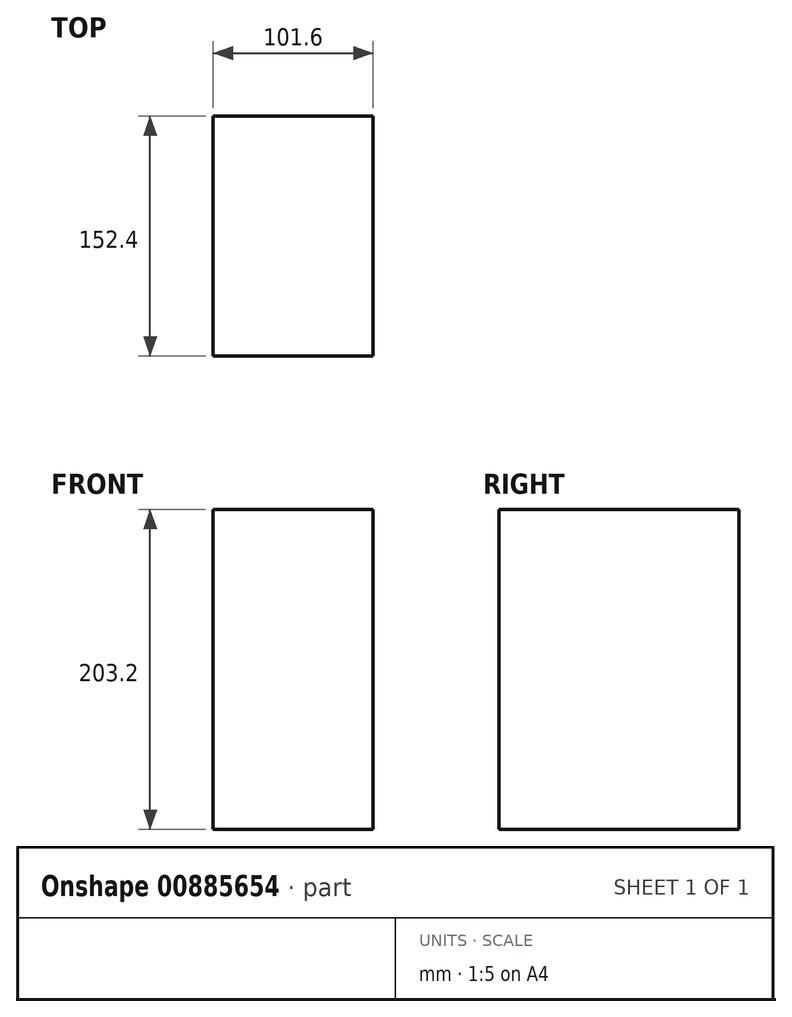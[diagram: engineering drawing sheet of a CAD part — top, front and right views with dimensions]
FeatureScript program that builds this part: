
annotation { "Feature Type Name" : "Feature", "Feature Type Description" : "" }
export const myFeature = defineFeature(function(context is Context, id is Id, definition is map)
    precondition{}
    {
        {
            var Q0;
            Q0=qCreatedBy(makeId("Top.planeOp"),FACE);
            var sketch = newSketch(context, id + "F0", { "sketchPlane" : qUnion([Q0])});
            skLineSegment(sketch, "E0.bottom", {"start": v(0, 0) * mm, "end": v(101.6, 0) * mm});
            skLineSegment(sketch, "E0.top", {"start": v(0, 152.4) * mm, "end": v(101.6, 152.4) * mm});
            skLineSegment(sketch, "E0.left", {"start": v(0, 0) * mm, "end": v(0, 152.4) * mm});
            skLineSegment(sketch, "E0.right", {"start": v(101.6, 0) * mm, "end": v(101.6, 152.4) * mm});
            skSolve(sketch);
        }
        {
            var Q0;
            Q0 = qSketchRegion(id + "F0", true);
            extrude(context, id + "F1", {"entities" : qUnion([Q0]), "depth" : 101.6 * mm, "offsetDistance" : 25.4 * mm});
        }
        {
            var Q0;
            Q0=makeQuery(id+"F1.opExtrude","SWEPT_BODY",BODY,{"disambiguationData":[OSD([sQuery(id+"F0.wireOp",EDGE,"E0.bottom"),sQuery(id+"F0.wireOp",EDGE,"E0.top"),sQuery(id+"F0.wireOp",EDGE,"E0.left"),sQuery(id+"F0.wireOp",EDGE,"E0.right")])]});
            var Q1;
            Q1=makeQuery(id+"F1.opExtrude","CAP_FACE",FACE,{"disambiguationData":[OSD([sQuery(id+"F0.wireOp",EDGE,"E0.bottom"),sQuery(id+"F0.wireOp",EDGE,"E0.top"),sQuery(id+"F0.wireOp",EDGE,"E0.left"),sQuery(id+"F0.wireOp",EDGE,"E0.right")])],"isStart":true});
            mirror(context, id + "F2", {"operationType" : NewBodyOperationType.ADD, "entities" : qUnion([Q0]), "mirrorPlane" : qUnion([Q1])});
        }
    });
